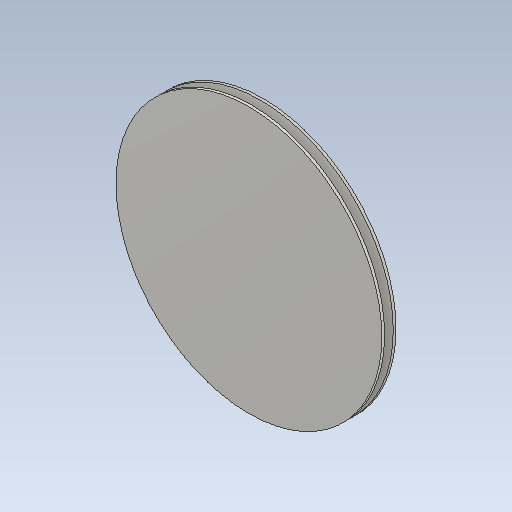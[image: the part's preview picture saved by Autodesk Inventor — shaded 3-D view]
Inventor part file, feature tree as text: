
AUTODESK INVENTOR PART (.ipt)
format: ipt  version: 2020.5 (Build 245400000, 400)  size: 113,152 bytes
history: native  units: mm (DEFAULTED — no unit token found)
features: other x3, fillet x2, sketch x1, pattern_linear x1
ambient origin geometry x8: Origin, YZ Plane, XZ Plane, XY Plane, X Axis, Y Axis, Z Axis, Center Point
bodies: Solid1 (feature_tree)
feature tree (7):
  sketch  "Boceto principal"  dims[d2=2.0mm d5=8.0mm d6=16.0mm d7=90.0deg d8=0.0mm d9=0.0mm d10=0.0mm d11=0.0mm d15=90.0deg d16=10.0mm d18=12.0mm d21=295.0mm d24=0.0mm d25=11.0mm d26=0.0mm d27=8.0mm]
  other  "Plano de correa"
  other  "Cuerpo"
  other  "Para ranuras"
  fillet  "Empalme externo"  Radius=8.5mm
  fillet  "Empalme interno"  Radius=5.934119mm
  pattern_linear  "Patrón para ranuras"  Spacing1=8.0mm  [1 undecoded]
note: 1 required parameter value undecoded (feature->parameter linkage not recoverable at this tier; creation-order binding heuristic only, values carry confidence <= 0.55)
